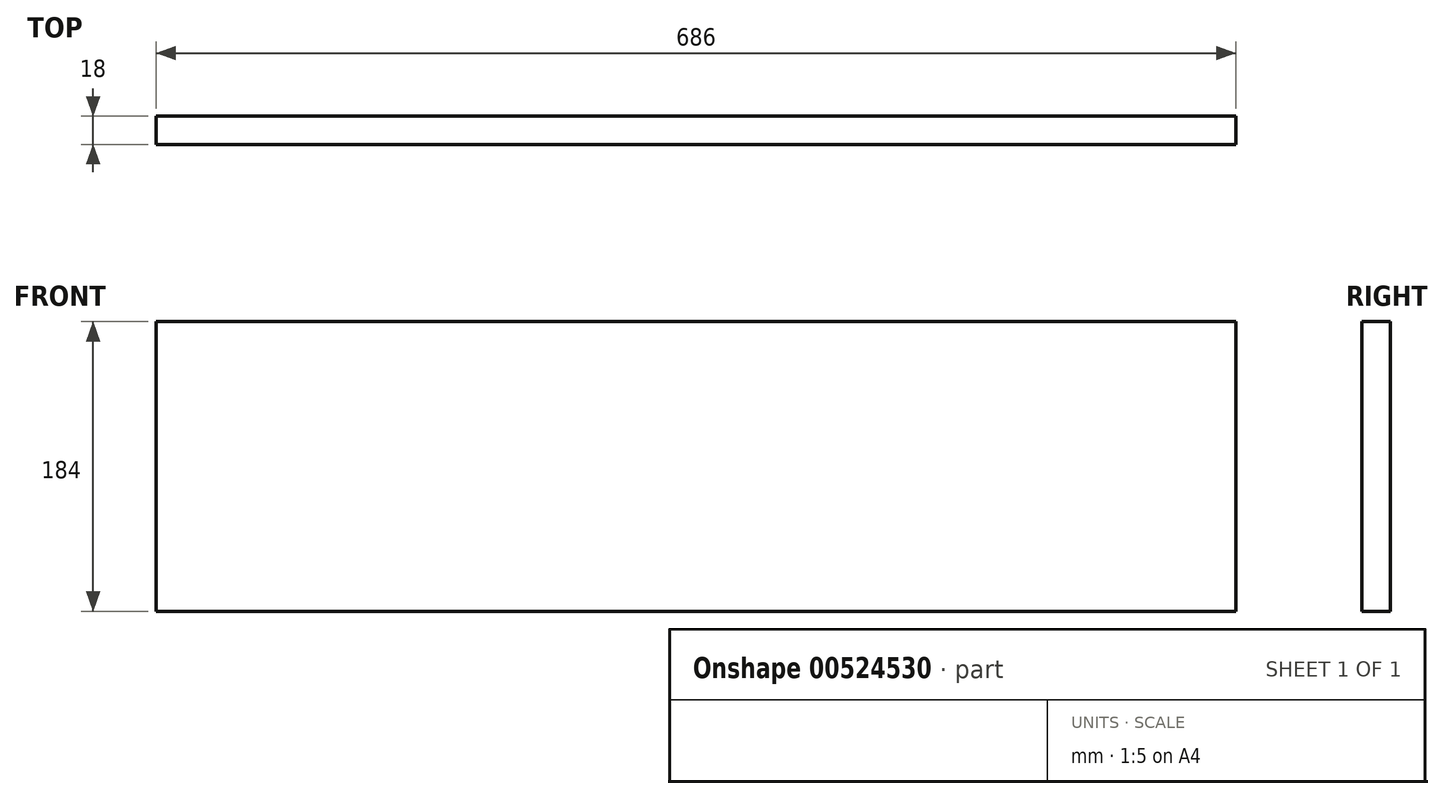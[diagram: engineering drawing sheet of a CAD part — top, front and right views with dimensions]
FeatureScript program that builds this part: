
annotation { "Feature Type Name" : "Feature", "Feature Type Description" : "" }
export const myFeature = defineFeature(function(context is Context, id is Id, definition is map)
    precondition{}
    {
        {
            var Q0;
            Q0=qCreatedBy(makeId("Front.planeOp"),FACE);
            var sketch = newSketch(context, id + "F0", { "sketchPlane" : qUnion([Q0])});
            skLineSegment(sketch, "E0.bottom", {"start": v(0, 0) * mm, "end": v(686, 0) * mm});
            skLineSegment(sketch, "E0.top", {"start": v(0, 184) * mm, "end": v(686, 184) * mm});
            skLineSegment(sketch, "E0.left", {"start": v(0, 0) * mm, "end": v(0, 184) * mm});
            skLineSegment(sketch, "E0.right", {"start": v(686, 0) * mm, "end": v(686, 184) * mm});
            skSolve(sketch);
        }
        {
            var Q0;
            Q0=qSketchRegion(id+"F0",true);
            extrude(context, id + "F1", {"entities" : qUnion([Q0]), "depth" : 18 * mm, "offsetDistance" : 25 * mm});
        }
    });
